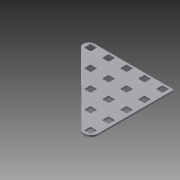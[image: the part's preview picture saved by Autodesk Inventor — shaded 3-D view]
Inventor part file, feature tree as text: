
AUTODESK INVENTOR PART (.ipt)
format: ipt  version: 2012 (Build 160160000, 160)  size: 1,277,440 bytes
history: native  units: in
note: dims shown in document units (in); Inventor stores cm internally (conversion verified against a paired STEP export)
features: plane x2, split x2, other x1, imported_body x1, extrude x1, sketch x1
ambient origin geometry x8: Origin, YZ Plane, XZ Plane, XY Plane, X Axis, Y Axis, Z Axis, Center Point
feature tree (8):
  parser-record x1  (decoder bookkeeping rows leaked as tree rows — omitted from the tree; the rows remain in map.json)
  imported_body  "Base1"
  extrude  "Extrusion1"  [1 undecoded]
  plane  "Work Plane1"
  split  "Split1"
  plane  "Work Plane2"
  split  "Split2"
  sketch  "Sketch1"  dims[d0=1.0in d1=0.0in]
note: 1 required parameter value undecoded (feature->parameter linkage not recoverable at this tier; creation-order binding heuristic only, values carry confidence <= 0.55)
